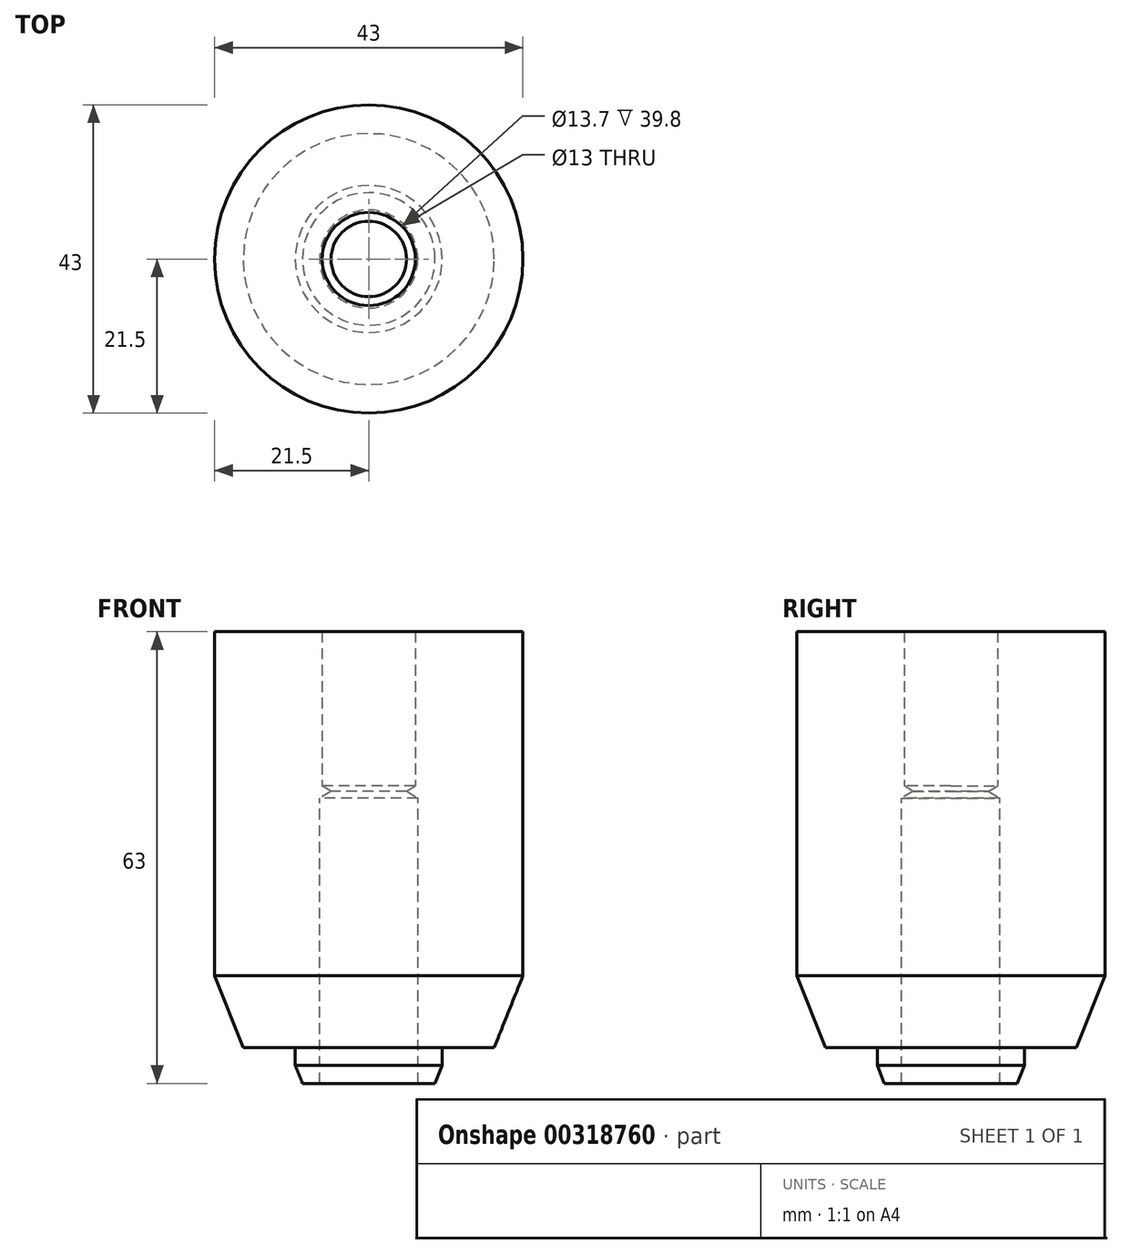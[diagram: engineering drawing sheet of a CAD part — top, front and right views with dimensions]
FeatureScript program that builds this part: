
annotation { "Feature Type Name" : "Feature", "Feature Type Description" : "" }
export const myFeature = defineFeature(function(context is Context, id is Id, definition is map)
    precondition{}
    {
        {
            var Q0;
            Q0=qCreatedBy(makeId("Top.planeOp"),FACE);
            var sketch = newSketch(context, id + "F0", { "sketchPlane" : qUnion([Q0])});
            skCircle(sketch, "E0", {"center": v(0, 0) * mm, "radius": 21.5 * mm});
            skSolve(sketch);
        }
        {
            var Q0;
            Q0=makeQuery(id+"F0.imprint","IMPRINT",FACE,{"disambiguationData":[TD([[makeQuery(id+"F0.imprint","IMPRINT",EDGE,{"derivedFrom":sQuery(id+"F0.wireOp",EDGE,"E0")}),1.0]])]});
            extrude(context, id + "F1", {"entities" : qUnion([Q0]), "oppositeDirection" : true, "depth" : 58 * mm});
        }
        {
            var Q0;
            Q0=makeQuery(id+"F1.opExtrude","CAP_EDGE",EDGE,{"disambiguationData":[OSD([sQuery(id+"F0.wireOp",EDGE,"E0")])],"isStart":false});
            chamfer(context, id + "F2", {"entities" : qUnion([Q0]), "chamferType" : ChamferType.TWO_OFFSETS, "width1" : 10 * mm, "oppositeDirection" : false, "width2" : 4 * mm, "tangentPropagation" : true});
        }
        {
            var Q0;
            Q0=makeQuery(id+"F1.opExtrude","CAP_FACE",FACE,{"disambiguationData":[OSD([sQuery(id+"F0.wireOp",EDGE,"E0")])],"isStart":false});
            var sketch = newSketch(context, id + "F3", { "sketchPlane" : qUnion([Q0])});
            skCircle(sketch, "E1", {"center": v(0, 0) * mm, "radius": 6.85 * mm});
            skSolve(sketch);
        }
        {
            var Q0;
            Q0=sQuery(id+"F3.wireOp",VERTEX,"E1.center");
            var Q1;
            Q1=makeQuery(id+"F1.opExtrude","SWEPT_BODY",BODY,{"disambiguationData":[OSD([sQuery(id+"F0.wireOp",EDGE,"E0")])]});
            hole(context, id + "F4", {"style" : HoleStyle.SIMPLE, "endStyle" : HoleEndStyle.BLIND, "holeDiameter" : 13.7 * mm, "holeDepth" : 34.8 * mm, "tappedDepth" : 12 * mm, "tapClearance" : 3, "locations" : qUnion([Q0]), "scope" : qUnion([Q1])});
        }
        {
            var Q0;
            Q0=makeQuery(id+"F1.opExtrude","CAP_FACE",FACE,{"disambiguationData":[OSD([sQuery(id+"F0.wireOp",EDGE,"E0")])],"isStart":true});
            var sketch = newSketch(context, id + "F5", { "sketchPlane" : qUnion([Q0])});
            skCircle(sketch, "E2", {"center": v(0, 0) * mm, "radius": 6.5 * mm});
            skSolve(sketch);
        }
        {
            var Q0;
            Q0=sQuery(id+"F5.wireOp",VERTEX,"E2.center");
            var Q1;
            Q1=makeQuery(id+"F1.opExtrude","SWEPT_BODY",BODY,{"disambiguationData":[OSD([sQuery(id+"F0.wireOp",EDGE,"E0")])]});
            hole(context, id + "F6", {"style" : HoleStyle.SIMPLE, "endStyle" : HoleEndStyle.BLIND, "holeDiameter" : 13 * mm, "holeDepth" : 21.5 * mm, "tappedDepth" : 12 * mm, "tapClearance" : 3, "locations" : qUnion([Q0]), "scope" : qUnion([Q1])});
        }
        {
            var Q0;
            Q0=makeQuery(id+"F1.opExtrude","CAP_FACE",FACE,{"disambiguationData":[OSD([sQuery(id+"F0.wireOp",EDGE,"E0")])],"isStart":false});
            var sketch = newSketch(context, id + "F7", { "sketchPlane" : qUnion([Q0])});
            skCircle(sketch, "E3", {"center": v(0, 0) * mm, "radius": 10.25 * mm});
            skCircle(sketch, "E4", {"center": v(0, 0) * mm, "radius": 6.85 * mm});
            skSolve(sketch);
        }
        {
            var Q0;
            Q0=makeQuery(id+"F7.imprint","IMPRINT",FACE,{"disambiguationData":[TD([[makeQuery(id+"F7.imprint","IMPRINT",EDGE,{"derivedFrom":sQuery(id+"F7.wireOp",EDGE,"E3")}),1.0]])]});
            extrude(context, id + "F8", {"entities" : qUnion([Q0]), "operationType" : NewBodyOperationType.ADD, "depth" : 5 * mm});
        }
        {
            var Q0;
            Q0=makeQuery(id+"F8.opExtrude","CAP_EDGE",EDGE,{"disambiguationData":[OSD([sQuery(id+"F7.wireOp",EDGE,"E3")])],"isStart":false});
            chamfer(context, id + "F9", {"entities" : qUnion([Q0]), "chamferType" : ChamferType.TWO_OFFSETS, "width1" : 1 * mm, "oppositeDirection" : false, "width2" : 2.5 * mm, "tangentPropagation" : true});
        }
    });
